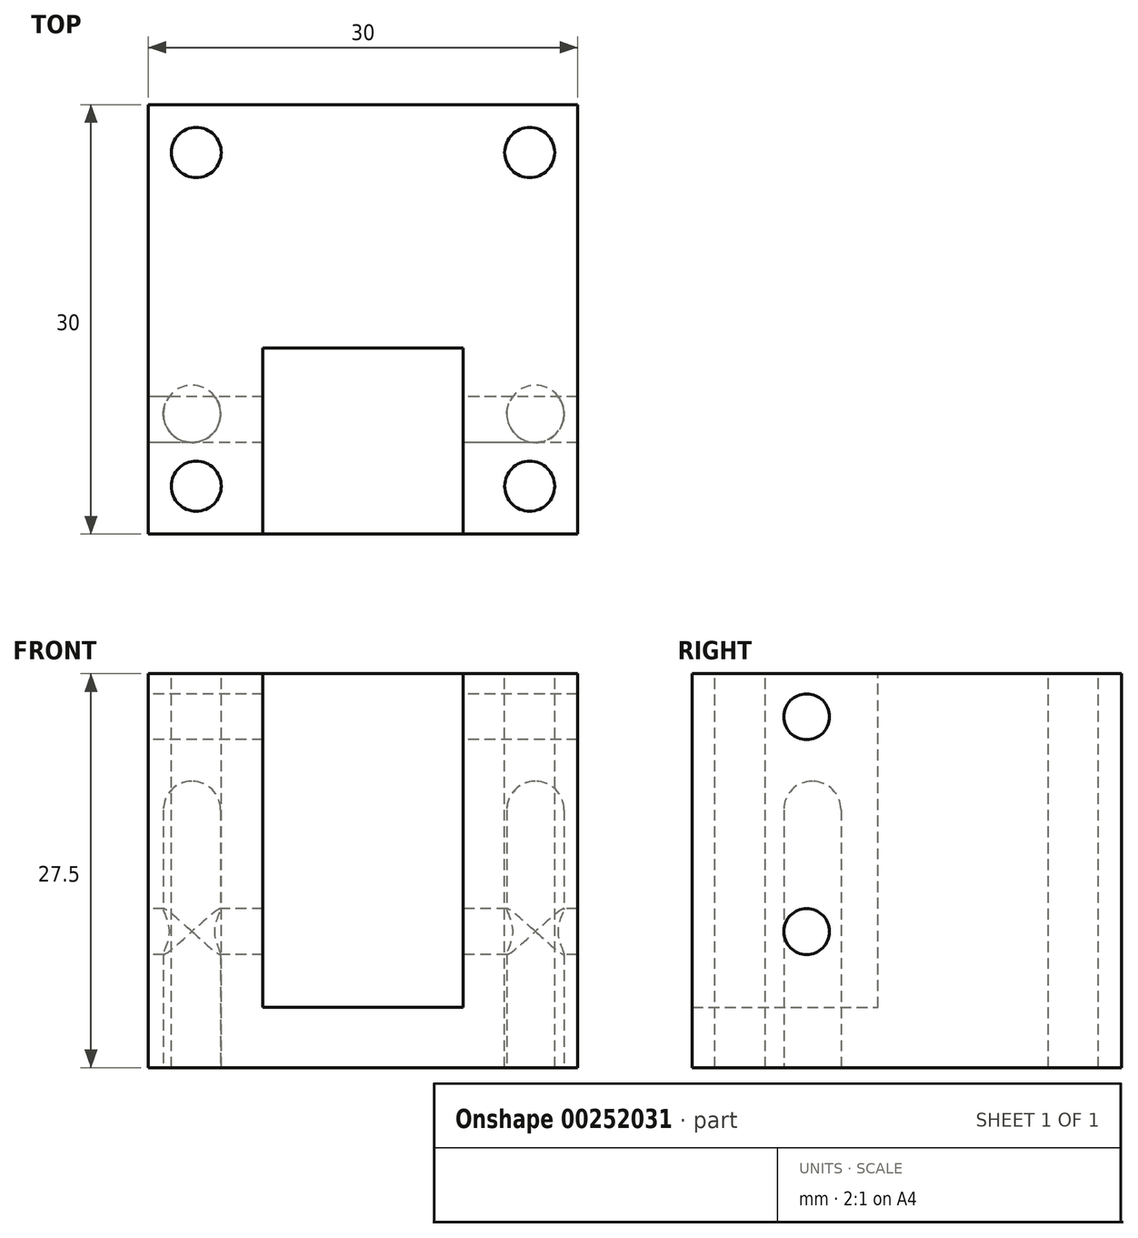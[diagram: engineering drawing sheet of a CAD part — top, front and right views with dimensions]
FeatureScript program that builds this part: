
annotation { "Feature Type Name" : "Feature", "Feature Type Description" : "" }
export const myFeature = defineFeature(function(context is Context, id is Id, definition is map)
    precondition{}
    {
        {
            var Q0;
            Q0=qCreatedBy(makeId("Top.planeOp"),FACE);
            var sketch = newSketch(context, id + "F0", { "sketchPlane" : qUnion([Q0])});
            skLineSegment(sketch, "E0.bottom", {"start": v(15, -15) * mm, "end": v(-15, -15) * mm});
            skLineSegment(sketch, "E0.top", {"start": v(15, 15) * mm, "end": v(-15, 15) * mm});
            skLineSegment(sketch, "E0.left", {"start": v(15, -15) * mm, "end": v(15, 15) * mm});
            skLineSegment(sketch, "E0.right", {"start": v(-15, -15) * mm, "end": v(-15, 15) * mm});
            skPoint(sketch, "E0.middle", {"position": v(0, 0) * mm});
            skSolve(sketch);
        }
        {
            var Q0;
            Q0=qSketchRegion(id+"F0",true);
            extrude(context, id + "F1", {"entities" : qUnion([Q0]), "depth" : 27.5 * mm});
        }
        {
            var Q0;
            {var subQ0=sQuery(id+"F0.wireOp",EDGE,"E0.bottom");var subQ1=sQuery(id+"F0.wireOp",EDGE,"E0.right");var subQ2=sQuery(id+"F0.wireOp",EDGE,"E0.top");Q0=makeQuery(id+"FrSbJtTGU18DsIY_1.boolean.opBoolean","SPLIT",FACE,{"disambiguationData":[TD([makeQuery(id+"F1.opExtrude","SWEPT_FACE",FACE,{"disambiguationData":[OSD([subQ1])]})])],"derivedFrom":makeQuery(id+"F1.opExtrude","CAP_FACE",FACE,{"disambiguationData":[OSD([subQ0,subQ2,sQuery(id+"F0.wireOp",EDGE,"E0.left"),subQ1])],"isStart":false})});}
            var sketch = newSketch(context, id + "F2", { "sketchPlane" : qUnion([Q0])});
            skCircle(sketch, "E1", {"center": v(-11.65, 11.65) * mm, "radius": 1.75 * mm});
            skCircle(sketch, "E2", {"center": v(-11.65, -11.65) * mm, "radius": 1.75 * mm});
            skCircle(sketch, "E3", {"center": v(11.65, 11.65) * mm, "radius": 1.75 * mm});
            skCircle(sketch, "E4", {"center": v(11.65, -11.65) * mm, "radius": 1.75 * mm});
            skSolve(sketch);
        }
        {
            var Q0;
            Q0=qSketchRegion(id+"F2",true);
            extrude(context, id + "F3", {"entities" : qUnion([Q0]), "operationType" : NewBodyOperationType.REMOVE, "endBound" : BoundingType.THROUGH_ALL, "oppositeDirection" : true, "depth" : 25 * mm});
        }
        {
            var Q0;
            Q0=makeQuery(id+"F1.opExtrude","CAP_FACE",FACE,{"disambiguationData":[OSD([sQuery(id+"F0.wireOp",EDGE,"E0.bottom"),sQuery(id+"F0.wireOp",EDGE,"E0.top"),sQuery(id+"F0.wireOp",EDGE,"E0.left"),sQuery(id+"F0.wireOp",EDGE,"E0.right")])],"isStart":true});
            var sketch = newSketch(context, id + "F4", { "sketchPlane" : qUnion([Q0])});
            skCircle(sketch, "E5", {"center": v(-11.95, 6.6) * mm, "radius": 2 * mm});
            skCircle(sketch, "E6", {"center": v(12.05, 6.6) * mm, "radius": 2 * mm});
            skSolve(sketch);
        }
        {
            var Q0;
            Q0=qSketchRegion(id+"F4",true);
            extrude(context, id + "F5", {"entities" : qUnion([Q0]), "operationType" : NewBodyOperationType.REMOVE, "oppositeDirection" : true, "depth" : 20 * mm});
        }
        {
            var Q0;
            Q0=makeQuery(id+"F5.boolean.opBoolean","COPY",FACE,{"derivedFrom":makeQuery(id+"F5.opExtrude","CAP_FACE",FACE,{"disambiguationData":[OSD([sQuery(id+"F4.wireOp",EDGE,"E5")])],"isStart":false})});
            var Q1;
            Q1=makeQuery(id+"F5.boolean.opBoolean","COPY",FACE,{"derivedFrom":makeQuery(id+"F5.opExtrude","CAP_FACE",FACE,{"disambiguationData":[OSD([sQuery(id+"F4.wireOp",EDGE,"sZuY8GY9-i2bP-Fcrm-ONg3-wngFPy5apMYd")])],"isStart":false})});
            var Q2;
            Q2=makeQuery(id+"F5.boolean.opBoolean","COPY",FACE,{"derivedFrom":makeQuery(id+"F5.opExtrude","CAP_FACE",FACE,{"disambiguationData":[OSD([sQuery(id+"F4.wireOp",EDGE,"E6")])],"isStart":false})});
            var Q3;
            Q3=makeQuery(id+"F5.boolean.opBoolean","COPY",FACE,{"derivedFrom":makeQuery(id+"F5.opExtrude","CAP_FACE",FACE,{"disambiguationData":[OSD([sQuery(id+"F4.wireOp",EDGE,"QC5nrsWR-ocza-fEwp-D0e1-ZJdKuwugIYmd")])],"isStart":false})});
            fillet(context, id + "F6", {"entities" : qUnion([Q0, Q1, Q2, Q3]), "radius" : 2 * mm, "tangentPropagation" : true, "allowEdgeOverflow" : false});
        }
        {
            var Q0;
            Q0=makeQuery(id+"F1.opExtrude","CAP_FACE",FACE,{"disambiguationData":[OSD([sQuery(id+"F0.wireOp",EDGE,"E0.bottom"),sQuery(id+"F0.wireOp",EDGE,"E0.top"),sQuery(id+"F0.wireOp",EDGE,"E0.left"),sQuery(id+"F0.wireOp",EDGE,"E0.right")])],"isStart":false});
            var sketch = newSketch(context, id + "F7", { "sketchPlane" : qUnion([Q0])});
            skLineSegment(sketch, "E7.bottom", {"start": v(-7, -15) * mm, "end": v(7, -15) * mm});
            skLineSegment(sketch, "E7.top", {"start": v(-7, -2) * mm, "end": v(7, -2) * mm});
            skLineSegment(sketch, "E7.left", {"start": v(-7, -15) * mm, "end": v(-7, -2) * mm});
            skLineSegment(sketch, "E7.right", {"start": v(7, -15) * mm, "end": v(7, -2) * mm});
            skSolve(sketch);
        }
        {
            var Q0;
            Q0=makeQuery(id+"F7.imprint","IMPRINT",FACE,{"disambiguationData":[TD([[makeQuery(id+"F7.imprint","IMPRINT",EDGE,{"derivedFrom":sQuery(id+"F7.wireOp",EDGE,"E7.bottom")}),-1.0]])]});
            extrude(context, id + "F8", {"entities" : qUnion([Q0]), "operationType" : NewBodyOperationType.REMOVE, "oppositeDirection" : true, "depth" : 23.3 * mm});
        }
        {
            var Q0;
            Q0=makeQuery(id+"F1.opExtrude","SWEPT_FACE",FACE,{"disambiguationData":[OSD([sQuery(id+"F0.wireOp",EDGE,"E0.right")])]});
            var sketch = newSketch(context, id + "F9", { "sketchPlane" : qUnion([Q0])});
            skCircle(sketch, "E8", {"center": v(7, 9.5) * mm, "radius": 1.6 * mm});
            skCircle(sketch, "E9", {"center": v(7, 24.5) * mm, "radius": 1.6 * mm});
            skSolve(sketch);
        }
        {
            var Q0;
            Q0 = qSketchRegion(id + "F9", true);
            extrude(context, id + "F10", {"entities" : qUnion([Q0]), "operationType" : NewBodyOperationType.REMOVE, "endBound" : BoundingType.THROUGH_ALL, "oppositeDirection" : true, "depth" : 25 * mm});
        }
    });
